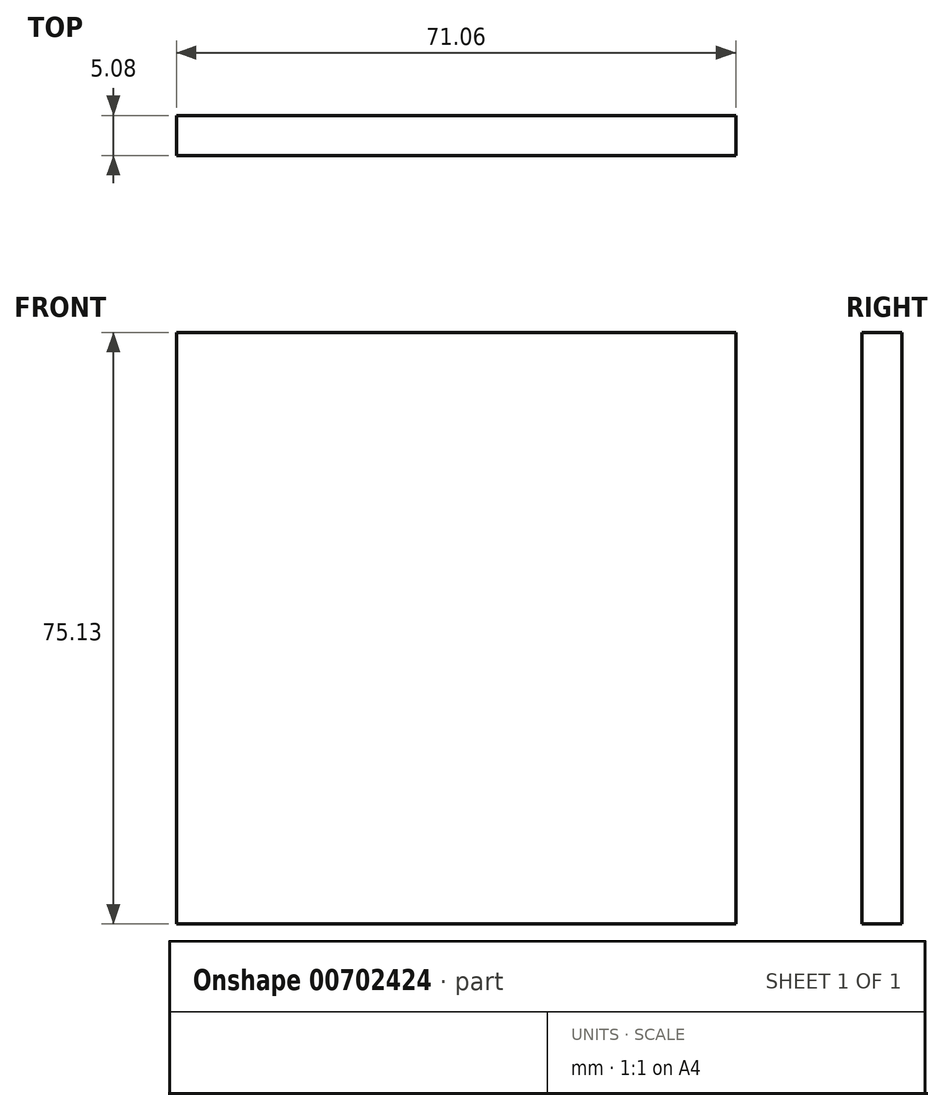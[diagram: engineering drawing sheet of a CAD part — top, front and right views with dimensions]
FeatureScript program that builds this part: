
annotation { "Feature Type Name" : "Feature", "Feature Type Description" : "" }
export const myFeature = defineFeature(function(context is Context, id is Id, definition is map)
    precondition{}
    {
        {
            var Q0;
            Q0=qCreatedBy(makeId("Front.planeOp"),FACE);
            var sketch = newSketch(context, id + "F0", { "sketchPlane" : qUnion([Q0])});
            skLineSegment(sketch, "E0.top", {"start": v(35.53, 49.38) * mm, "end": v(-35.53, 49.38) * mm});
            skLineSegment(sketch, "E0.left", {"start": v(35.53, -25.75) * mm, "end": v(35.53, 49.38) * mm});
            skLineSegment(sketch, "E0.right", {"start": v(-35.53, -25.75) * mm, "end": v(-35.53, 49.38) * mm});
            skPoint(sketch, "E0.middle", {"position": v(0, 0) * mm});
            skPoint(sketch, "E1.orphan", {"position": v(-35.53, -49.38) * mm});
            skPoint(sketch, "E2.orphan", {"position": v(35.53, -49.38) * mm});
            skLineSegment(sketch, "E3", {"start": v(-35.53, -25.75) * mm, "end": v(35.53, -25.75) * mm});
            skSolve(sketch);
        }
        {
            var Q0;
            Q0 = qSketchRegion(id + "F0", true);
            extrude(context, id + "F1", {"entities" : qUnion([Q0]), "depth" : 5.08 * mm, "offsetDistance" : 25.4 * mm});
        }
    });
